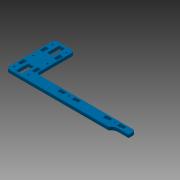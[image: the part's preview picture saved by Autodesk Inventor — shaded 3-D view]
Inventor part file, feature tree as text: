
AUTODESK INVENTOR PART (.ipt)
format: ipt  version: 2013 (Build 170138000, 138)  size: 147,456 bytes
history: native  units: mm
features: extrude x1, sketch x1
ambient origin geometry x8: Origin, YZ Plane, XZ Plane, XY Plane, X Axis, Y Axis, Z Axis, Center Point
bodies: Solid1 (feature_tree)
feature tree (2):
  extrude  "Extrusion1"  [1 undecoded]
  sketch  "Sketch1"  dims[d0=6.0mm d1=0.0mm]
note: 1 required parameter value undecoded (feature->parameter linkage not recoverable at this tier; creation-order binding heuristic only, values carry confidence <= 0.55)
